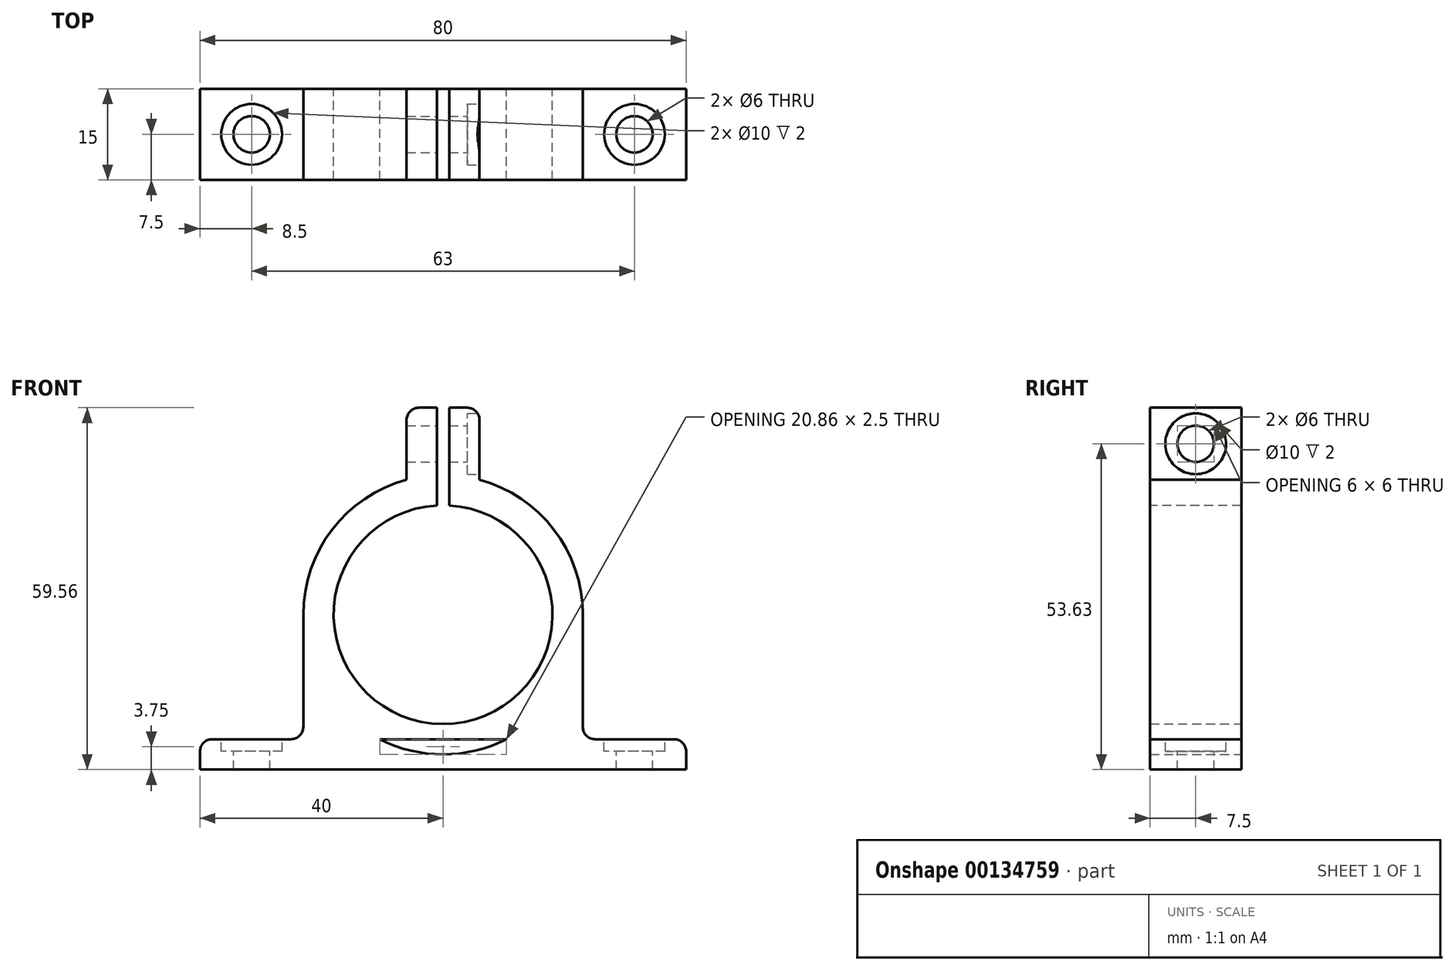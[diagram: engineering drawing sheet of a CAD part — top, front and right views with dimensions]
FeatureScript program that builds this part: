
annotation { "Feature Type Name" : "Feature", "Feature Type Description" : "" }
export const myFeature = defineFeature(function(context is Context, id is Id, definition is map)
    precondition{}
    {
        {
            var Q0;
            Q0=qCreatedBy(makeId("Front.planeOp"),FACE);
            var sketch = newSketch(context, id + "F0", { "sketchPlane" : qUnion([Q0])});
            skCircle(sketch, "E0", {"center": v(0, 0) * mm, "radius": 18 * mm});
            skCircle(sketch, "E1.0", {"center": v(0, 0) * mm, "radius": 23 * mm});
            skLineSegment(sketch, "E2.bottom", {"start": v(40, -25.5) * mm, "end": v(-40, -25.5) * mm});
            skLineSegment(sketch, "E2.top", {"start": v(40, -20.5) * mm, "end": v(-40, -20.5) * mm});
            skLineSegment(sketch, "E2.left", {"start": v(40, -25.5) * mm, "end": v(40, -20.5) * mm});
            skLineSegment(sketch, "E2.right", {"start": v(-40, -25.5) * mm, "end": v(-40, -20.5) * mm});
            skPoint(sketch, "E2.middle", {"position": v(0, -23) * mm});
            skLineSegment(sketch, "E3", {"start": v(-23, 0) * mm, "end": v(-23, -20.5) * mm});
            skLineSegment(sketch, "E4", {"start": v(23, 0) * mm, "end": v(23, -20.5) * mm});
            skLineSegment(sketch, "E5.bottom", {"start": v(6, 34.06) * mm, "end": v(-6, 34.06) * mm});
            skLineSegment(sketch, "E5.top", {"start": v(6, 19.06) * mm, "end": v(-6, 19.06) * mm});
            skLineSegment(sketch, "E5.left", {"start": v(6, 34.06) * mm, "end": v(6, 19.06) * mm});
            skLineSegment(sketch, "E5.right", {"start": v(-6, 34.06) * mm, "end": v(-6, 19.06) * mm});
            skPoint(sketch, "E5.middle", {"position": v(0, 26.56) * mm});
            skSolve(sketch);
        }
        {
            var Q0;
            Q0=makeQuery(id+"F0.imprint","IMPRINT",FACE,{"disambiguationData":[TD([[makeQuery(id+"F0.imprint","IMPRINT",EDGE,{"derivedFrom":sQuery(id+"F0.wireOp",EDGE,"E2.bottom")}),-1.0]])]});
            var Q1;
            {var subQ0=sQuery(id+"F0.wireOp",EDGE,"E3");Q1=makeQuery(id+"F0.imprint","IMPRINT",FACE,{"disambiguationData":[TD([[makeQuery(id+"F0.imprint","IMPRINT",EDGE,{"derivedFrom":subQ0}),1.0]])]});}
            var Q2;
            Q2=makeQuery(id+"F0.imprint","IMPRINT",FACE,{"disambiguationData":[TD([[makeQuery(id+"F0.imprint","IMPRINT",EDGE,{"derivedFrom":sQuery(id+"F0.wireOp",EDGE,"E0")}),-1.0]])]});
            var Q3;
            {var subQ0=sQuery(id+"F0.wireOp",EDGE,"E4");Q3=makeQuery(id+"F0.imprint","IMPRINT",FACE,{"disambiguationData":[TD([[makeQuery(id+"F0.imprint","IMPRINT",EDGE,{"derivedFrom":subQ0}),-1.0]])]});}
            var Q4;
            {var subQ0=sQuery(id+"F0.wireOp",EDGE,"E2.top");var subQ1=sQuery(id+"F0.wireOp",EDGE,"E1.0");var subQ2=makeQuery(id+"F0.imprint","INTERSECT",VERTEX,{"disambiguationData":[OD(0.0)],"derivedFrom":[subQ1,subQ0]});Q4=makeQuery(id+"F0.imprint","IMPRINT",FACE,{"disambiguationData":[TD([[makeQuery(id+"F0.imprint","IMPRINT",EDGE,{"disambiguationData":[TD([[subQ2,-1.0]])],"derivedFrom":subQ1}),1.0]])]});}
            var Q5;
            {var subQ5=sQuery(id+"F0.wireOp",EDGE,"E5.bottom");Q5=makeQuery(id+"F0.imprint","IMPRINT",FACE,{"disambiguationData":[TD([[makeQuery(id+"F0.imprint","IMPRINT",EDGE,{"derivedFrom":subQ5}),1.0]])]});}
            var Q6;
            {var subQ5=sQuery(id+"F0.wireOp",EDGE,"E5.top");Q6=makeQuery(id+"F0.imprint","IMPRINT",FACE,{"disambiguationData":[TD([[makeQuery(id+"F0.imprint","IMPRINT",EDGE,{"derivedFrom":subQ5}),-1.0]])]});}
            extrude(context, id + "F1", {"entities" : qUnion([Q0, Q1, Q2, Q3, Q4, Q5, Q6]), "depth" : 15 * mm});
        }
        {
            var Q0;
            Q0=makeQuery(id+"F1.opExtrude","CAP_FACE",FACE,{"disambiguationData":[OSD([sQuery(id+"F0.wireOp",EDGE,"E0"),sQuery(id+"F0.wireOp",EDGE,"E1.0"),sQuery(id+"F0.wireOp",EDGE,"E2.bottom"),sQuery(id+"F0.wireOp",EDGE,"E2.top"),sQuery(id+"F0.wireOp",EDGE,"E2.left"),sQuery(id+"F0.wireOp",EDGE,"E2.right"),sQuery(id+"F0.wireOp",EDGE,"E3"),sQuery(id+"F0.wireOp",EDGE,"E4"),sQuery(id+"F0.wireOp",EDGE,"E5.bottom"),sQuery(id+"F0.wireOp",EDGE,"E5.left"),sQuery(id+"F0.wireOp",EDGE,"E5.right")])],"isStart":false});
            var sketch = newSketch(context, id + "F2", { "sketchPlane" : qUnion([Q0])});
            skLineSegment(sketch, "E6", {"start": v(0, -29.71) * mm, "end": v(0, 55.84) * mm, "construction": true});
            skPoint(sketch, "E6.endSnap0", {"position": v(0, -25.5) * mm});
            skLineSegment(sketch, "E7", {"start": v(-1, 34.06) * mm, "end": v(-1, 17.97) * mm});
            skLineSegment(sketch, "E8.MirrorCS", {"start": v(1, 34.06) * mm, "end": v(1, 17.97) * mm});
            skSolve(sketch);
        }
        {
            var Q0;
            {var subQ0=sQuery(id+"F2.wireOp",EDGE,"E7");Q0=makeQuery(id+"F2.imprint","IMPRINT",FACE,{"disambiguationData":[TD([[makeQuery(id+"F2.imprint","IMPRINT",EDGE,{"derivedFrom":subQ0}),1.0]])]});}
            extrude(context, id + "F3", {"entities" : qUnion([Q0]), "operationType" : NewBodyOperationType.REMOVE, "oppositeDirection" : true, "depth" : 25 * mm});
        }
        {
            var Q0;
            {var subQ0=sQuery(id+"F0.wireOp",EDGE,"E2.top");Q0=makeQuery(id+"F1.opExtrude","SWEPT_FACE",FACE,{"disambiguationData":[OSD([subQ0]),TDD([makeQuery(id+"F0.imprint","IMPRINT",EDGE,{"disambiguationData":[TD([[makeQuery(id+"F0.imprint","INTERSECT",VERTEX,{"derivedFrom":[subQ0,sQuery(id+"F0.wireOp",EDGE,"E2.left")]}),-1.0]])],"derivedFrom":subQ0})])]});}
            var sketch = newSketch(context, id + "F4", { "sketchPlane" : qUnion([Q0])});
            skLineSegment(sketch, "E9", {"start": v(23, -15) * mm, "end": v(40, 0) * mm, "construction": true});
            skLineSegment(sketch, "E10", {"start": v(40, 0) * mm, "end": v(40, -15) * mm, "construction": true});
            skLineSegment(sketch, "E11", {"start": v(40, -15) * mm, "end": v(23, 0) * mm, "construction": true});
            skCircle(sketch, "E12", {"center": v(31.5, -7.5) * mm, "radius": 3 * mm});
            skCircle(sketch, "E13.0", {"center": v(31.5, -7.5) * mm, "radius": 5 * mm});
            skSolve(sketch);
        }
        {
            var Q0;
            Q0=makeQuery(id+"F4.imprint","IMPRINT",FACE,{"disambiguationData":[TD([[makeQuery(id+"F4.imprint","IMPRINT",EDGE,{"derivedFrom":sQuery(id+"F4.wireOp",EDGE,"E12")}),1.0]])]});
            extrude(context, id + "F5", {"entities" : qUnion([Q0]), "operationType" : NewBodyOperationType.REMOVE, "oppositeDirection" : true, "depth" : 25 * mm});
        }
        {
            var Q0;
            Q0=makeQuery(id+"F4.imprint","IMPRINT",FACE,{"disambiguationData":[TD([[makeQuery(id+"F4.imprint","IMPRINT",EDGE,{"derivedFrom":sQuery(id+"F4.wireOp",EDGE,"E12")}),-1.0]])]});
            extrude(context, id + "F6", {"entities" : qUnion([Q0]), "operationType" : NewBodyOperationType.REMOVE, "oppositeDirection" : true, "depth" : 2 * mm});
        }
        {
            var Q0;
            {var subQ0=sQuery(id+"F0.wireOp",EDGE,"E2.top");Q0=makeQuery(id+"F1.opExtrude","SWEPT_FACE",FACE,{"disambiguationData":[OSD([subQ0]),TDD([makeQuery(id+"F0.imprint","IMPRINT",EDGE,{"disambiguationData":[TD([[makeQuery(id+"F0.imprint","INTERSECT",VERTEX,{"derivedFrom":[subQ0,sQuery(id+"F0.wireOp",EDGE,"E2.right")]}),1.0]])],"derivedFrom":subQ0})])]});}
            var sketch = newSketch(context, id + "F7", { "sketchPlane" : qUnion([Q0])});
            skLineSegment(sketch, "E14", {"start": v(-40, -15) * mm, "end": v(-23, 0) * mm, "construction": true});
            skLineSegment(sketch, "E15", {"start": v(-40, 0) * mm, "end": v(-23, -15) * mm, "construction": true});
            skCircle(sketch, "E16", {"center": v(-31.5, -7.5) * mm, "radius": 3 * mm});
            skCircle(sketch, "E17.0", {"center": v(-31.5, -7.5) * mm, "radius": 5 * mm});
            skSolve(sketch);
        }
        {
            var Q0;
            Q0=makeQuery(id+"F7.imprint","IMPRINT",FACE,{"disambiguationData":[TD([[makeQuery(id+"F7.imprint","IMPRINT",EDGE,{"derivedFrom":sQuery(id+"F7.wireOp",EDGE,"E16")}),1.0]])]});
            extrude(context, id + "F8", {"entities" : qUnion([Q0]), "operationType" : NewBodyOperationType.REMOVE, "oppositeDirection" : true, "depth" : 25 * mm});
        }
        {
            var Q0;
            Q0=makeQuery(id+"F7.imprint","IMPRINT",FACE,{"disambiguationData":[TD([[makeQuery(id+"F7.imprint","IMPRINT",EDGE,{"derivedFrom":sQuery(id+"F7.wireOp",EDGE,"E16")}),-1.0]])]});
            extrude(context, id + "F9", {"entities" : qUnion([Q0]), "operationType" : NewBodyOperationType.REMOVE, "oppositeDirection" : true, "depth" : 2 * mm});
        }
        {
            var Q0;
            Q0=makeQuery(id+"F1.opExtrude","SWEPT_FACE",FACE,{"disambiguationData":[OSD([sQuery(id+"F0.wireOp",EDGE,"E5.left")])]});
            var sketch = newSketch(context, id + "F10", { "sketchPlane" : qUnion([Q0])});
            skLineSegment(sketch, "E18", {"start": v(-15, 34.06) * mm, "end": v(0, 22.2) * mm, "construction": true});
            skLineSegment(sketch, "E19", {"start": v(-15, 22.2) * mm, "end": v(0, 34.06) * mm, "construction": true});
            skCircle(sketch, "E20", {"center": v(-7.5, 28.13) * mm, "radius": 3 * mm});
            skCircle(sketch, "E21.0", {"center": v(-7.5, 28.13) * mm, "radius": 5 * mm});
            skSolve(sketch);
        }
        {
            var Q0;
            Q0=makeQuery(id+"F10.imprint","IMPRINT",FACE,{"disambiguationData":[TD([[makeQuery(id+"F10.imprint","IMPRINT",EDGE,{"derivedFrom":sQuery(id+"F10.wireOp",EDGE,"E20")}),1.0]])]});
            extrude(context, id + "F11", {"entities" : qUnion([Q0]), "operationType" : NewBodyOperationType.REMOVE, "oppositeDirection" : true, "depth" : 25 * mm});
        }
        {
            var Q0;
            Q0=makeQuery(id+"F10.imprint","IMPRINT",FACE,{"disambiguationData":[TD([[makeQuery(id+"F10.imprint","IMPRINT",EDGE,{"derivedFrom":sQuery(id+"F10.wireOp",EDGE,"E20")}),-1.0]])]});
            extrude(context, id + "F12", {"entities" : qUnion([Q0]), "operationType" : NewBodyOperationType.REMOVE, "oppositeDirection" : true, "depth" : 2 * mm});
        }
        {
            var Q0;
            Q0=makeQuery(id+"F1.opExtrude","SWEPT_EDGE",EDGE,{"disambiguationData":[OSD([sQuery(id+"F0.wireOp",EDGE,"E2.top"),sQuery(id+"F0.wireOp",EDGE,"E4")])]});
            var Q1;
            Q1=makeQuery(id+"F1.opExtrude","SWEPT_EDGE",EDGE,{"disambiguationData":[OSD([sQuery(id+"F0.wireOp",EDGE,"E2.top"),sQuery(id+"F0.wireOp",EDGE,"E3")])]});
            var Q2;
            Q2=makeQuery(id+"F1.opExtrude","SWEPT_EDGE",EDGE,{"disambiguationData":[OSD([sQuery(id+"F0.wireOp",EDGE,"E5.bottom"),sQuery(id+"F0.wireOp",EDGE,"E5.right")])]});
            var Q3;
            Q3=makeQuery(id+"F1.opExtrude","SWEPT_EDGE",EDGE,{"disambiguationData":[OSD([sQuery(id+"F0.wireOp",EDGE,"E5.bottom"),sQuery(id+"F0.wireOp",EDGE,"E5.left")])]});
            var Q4;
            Q4=makeQuery(id+"F1.opExtrude","SWEPT_EDGE",EDGE,{"disambiguationData":[OSD([sQuery(id+"F0.wireOp",EDGE,"E2.top"),sQuery(id+"F0.wireOp",EDGE,"E2.left")])]});
            var Q5;
            Q5=makeQuery(id+"F1.opExtrude","SWEPT_EDGE",EDGE,{"disambiguationData":[OSD([sQuery(id+"F0.wireOp",EDGE,"E2.top"),sQuery(id+"F0.wireOp",EDGE,"E2.right")])]});
            fillet(context, id + "F13", {"entities" : qUnion([Q0, Q1, Q2, Q3, Q4, Q5]), "radius" : 2 * mm, "tangentPropagation" : true, "allowEdgeOverflow" : false});
        }
    });
